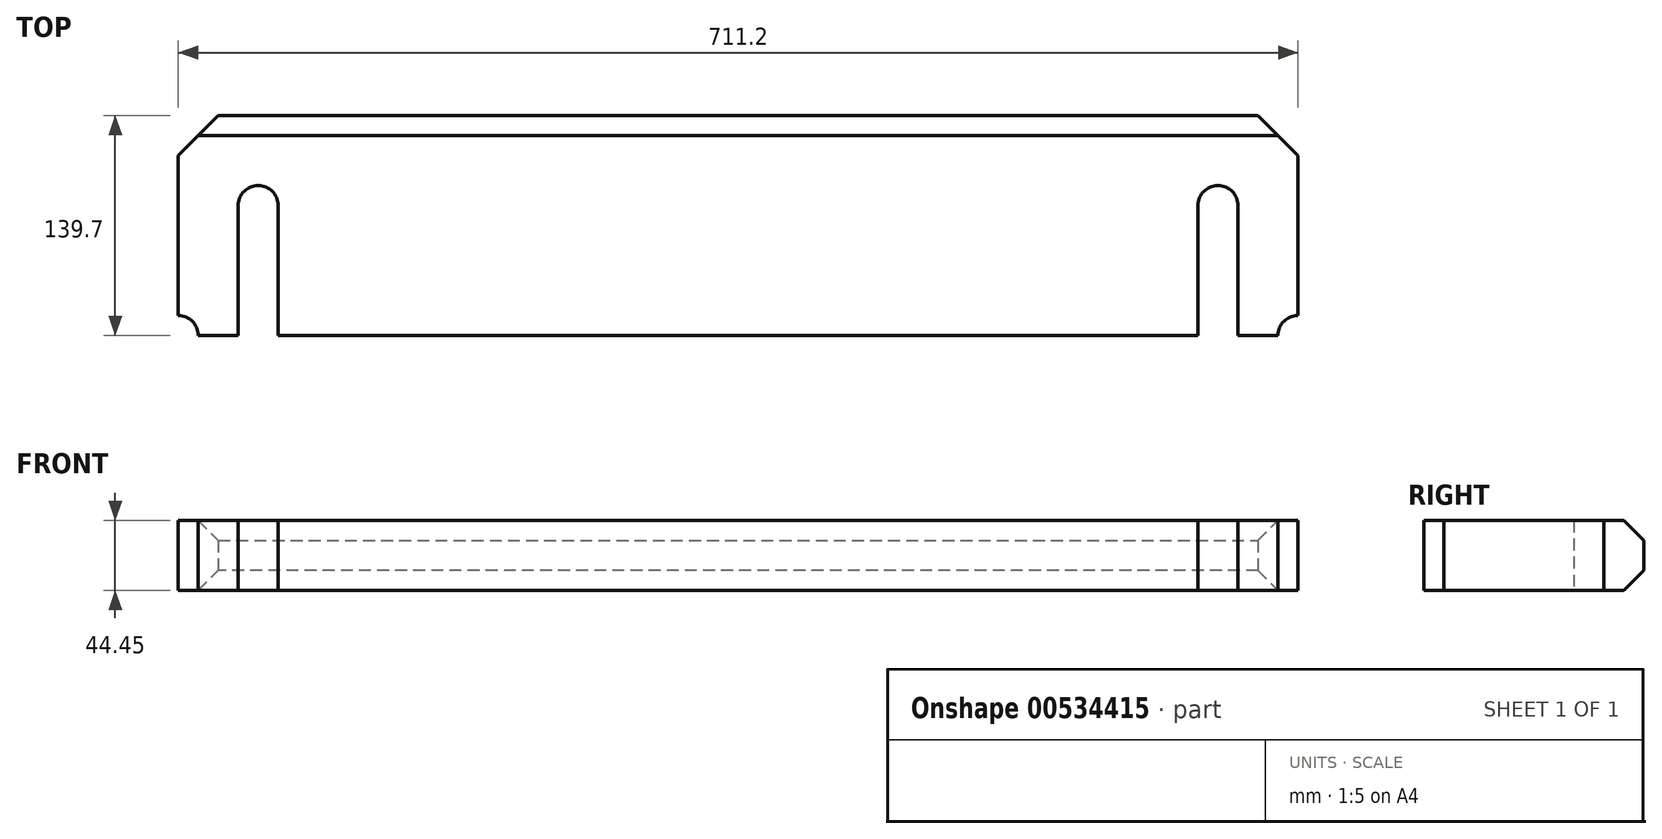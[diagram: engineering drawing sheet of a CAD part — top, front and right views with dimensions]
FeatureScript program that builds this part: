
annotation { "Feature Type Name" : "Feature", "Feature Type Description" : "" }
export const myFeature = defineFeature(function(context is Context, id is Id, definition is map)
    precondition{}
    {
        {
            var Q0;
            Q0=qCreatedBy(makeId("Top.planeOp"),FACE);
            var sketch = newSketch(context, id + "F0", { "sketchPlane" : qUnion([Q0])});
            skLineSegment(sketch, "E0", {"start": v(105.02, 139.7) * mm, "end": v(105.02, 0) * mm, "construction": true});
            skLineSegment(sketch, "E1", {"start": v(355.6, 157.39) * mm, "end": v(355.6, -27.96) * mm, "construction": true});
            skPoint(sketch, "E1.startSnap0", {"position": v(355.6, 139.7) * mm});
            skArc(sketch, "E2", {"start": v(63.5, 82.55) * mm, "mid": v(50.8, 95.25) * mm, "end": v(38.1, 82.55) * mm});
            skLineSegment(sketch, "E3", {"start": v(20.18, 82.55) * mm, "end": v(93.15, 82.55) * mm, "construction": true});
            skLineSegment(sketch, "E4", {"start": v(38.1, 82.55) * mm, "end": v(38.1, 0) * mm});
            skLineSegment(sketch, "E5", {"start": v(63.5, 82.55) * mm, "end": v(63.5, 0) * mm});
            skLineSegment(sketch, "E6", {"start": v(12.7, 0) * mm, "end": v(38.1, 0) * mm});
            skLineSegment(sketch, "E7", {"start": v(63.5, 0) * mm, "end": v(105.02, 0) * mm});
            skLineSegment(sketch, "E8", {"start": v(355.6, 0) * mm, "end": v(105.02, 0) * mm});
            skLineSegment(sketch, "E9", {"start": v(0, 114.3) * mm, "end": v(25.4, 139.7) * mm});
            skLineSegment(sketch, "E10", {"start": v(0, 12.7) * mm, "end": v(0, 114.3) * mm});
            skLineSegment(sketch, "E11", {"start": v(25.4, 139.7) * mm, "end": v(355.6, 139.7) * mm});
            skArc(sketch, "E12", {"start": v(12.7, 0) * mm, "mid": v(8.98, 8.98) * mm, "end": v(0, 12.7) * mm});
            skPoint(sketch, "E13.MirrorCS.start.orphan", {"position": v(355.6, 0) * mm});
            skLineSegment(sketch, "E14.MirrorCS", {"start": v(355.6, 0) * mm, "end": v(606.18, 0) * mm});
            skLineSegment(sketch, "E15.MirrorCS", {"start": v(685.8, 139.7) * mm, "end": v(355.6, 139.7) * mm});
            skLineSegment(sketch, "E16.MirrorCS", {"start": v(711.2, 114.3) * mm, "end": v(685.8, 139.7) * mm});
            skLineSegment(sketch, "E17.MirrorCS", {"start": v(711.2, 12.7) * mm, "end": v(711.2, 114.3) * mm});
            skArc(sketch, "E18.MirrorCS", {"start": v(698.5, 0) * mm, "mid": v(702.22, 8.98) * mm, "end": v(711.2, 12.7) * mm});
            skLineSegment(sketch, "E19.MirrorCS", {"start": v(698.5, 0) * mm, "end": v(673.1, 0) * mm});
            skLineSegment(sketch, "E20.MirrorCS", {"start": v(673.1, 82.55) * mm, "end": v(673.1, 0) * mm});
            skLineSegment(sketch, "E21.MirrorCS", {"start": v(647.7, 82.55) * mm, "end": v(647.7, 0) * mm});
            skLineSegment(sketch, "E22.MirrorCS", {"start": v(647.7, 0) * mm, "end": v(606.18, 0) * mm});
            skArc(sketch, "E23.MirrorCS", {"start": v(647.7, 82.55) * mm, "mid": v(660.4, 95.25) * mm, "end": v(673.1, 82.55) * mm});
            skSolve(sketch);
        }
        {
            var Q0;
            Q0 = qSketchRegion(id + "F0", true);
            extrude(context, id + "F1", {"entities" : qUnion([Q0]), "depth" : 44.45 * mm, "offsetDistance" : 25.4 * mm});
        }
        {
            var Q0;
            Q0=makeQuery(id+"F1.opExtrude","CAP_EDGE",EDGE,{"disambiguationData":[OSD([sQuery(id+"F0.wireOp",EDGE,"E11"),sQuery(id+"F0.wireOp",EDGE,"E15.MirrorCS")])],"isStart":false});
            var Q1;
            Q1=makeQuery(id+"F1.opExtrude","CAP_EDGE",EDGE,{"disambiguationData":[OSD([sQuery(id+"F0.wireOp",EDGE,"E11"),sQuery(id+"F0.wireOp",EDGE,"E15.MirrorCS")])],"isStart":true});
            chamfer(context, id + "F2", {"entities" : qUnion([Q0, Q1]), "width" : 12.7 * mm, "tangentPropagation" : true});
        }
    });
